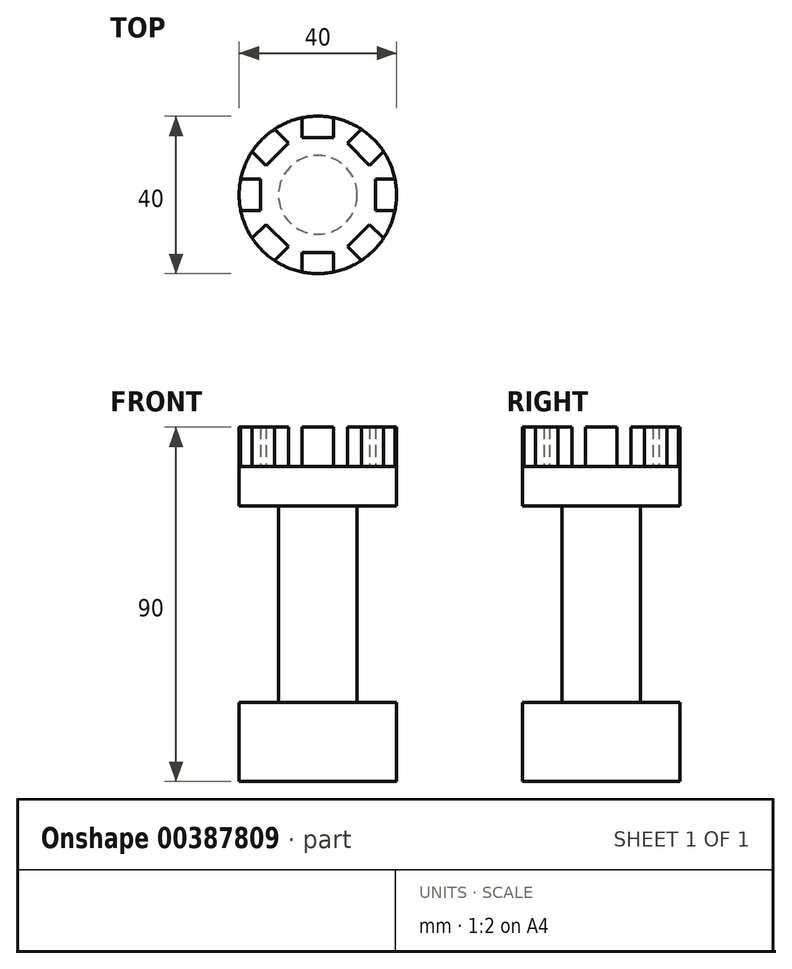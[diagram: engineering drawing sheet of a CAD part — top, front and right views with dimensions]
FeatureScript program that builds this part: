
annotation { "Feature Type Name" : "Feature", "Feature Type Description" : "" }
export const myFeature = defineFeature(function(context is Context, id is Id, definition is map)
    precondition{}
    {
        {
            var Q0;
            Q0=qCreatedBy(makeId("Front.planeOp"),FACE);
            var sketch = newSketch(context, id + "F0", { "sketchPlane" : qUnion([Q0])});
            skLineSegment(sketch, "E0", {"start": v(0, 64.98) * mm, "end": v(0, -64.38) * mm, "construction": true});
            skLineSegment(sketch, "E1", {"start": v(0, 40) * mm, "end": v(20, 40) * mm});
            skLineSegment(sketch, "E2", {"start": v(20, 30) * mm, "end": v(10, 30) * mm});
            skLineSegment(sketch, "E3", {"start": v(10, 30) * mm, "end": v(10, -20) * mm});
            skLineSegment(sketch, "E4", {"start": v(10, -20) * mm, "end": v(20, -20) * mm});
            skLineSegment(sketch, "E5", {"start": v(20, -20) * mm, "end": v(20, -40) * mm});
            skLineSegment(sketch, "E6", {"start": v(20, -40) * mm, "end": v(0, -40) * mm});
            skLineSegment(sketch, "E7", {"start": v(0, -40) * mm, "end": v(0, 40) * mm});
            skLineSegment(sketch, "E8", {"start": v(0, 40) * mm, "end": v(0, 40) * mm});
            skLineSegment(sketch, "E9", {"start": v(20, 40) * mm, "end": v(20, 30) * mm});
            skSolve(sketch);
        }
        {
            var Q0;
            Q0 = qSketchRegion(id + "F0", true);
            var Q1;
            Q1=sQuery(id+"F0.wireOp",EDGE,"E0");
            revolve(context, id + "F1", {"entities" : qUnion([Q0]), "axis" : qUnion([Q1]), "revolveType" : RevolveType.FULL});
        }
        {
            var Q0;
            Q0=makeQuery(id+"F1.opRevolve","SWEPT_FACE",FACE,{"disambiguationData":[OSD([sQuery(id+"F0.wireOp",EDGE,"E1")])]});
            var sketch = newSketch(context, id + "F2", { "sketchPlane" : qUnion([Q0])});
            skLineSegment(sketch, "E10", {"start": v(-4, 19.6) * mm, "end": v(-4, 14.6) * mm});
            skLineSegment(sketch, "E11", {"start": v(-4, 14.6) * mm, "end": v(4, 14.6) * mm});
            skLineSegment(sketch, "E12", {"start": v(4, 14.6) * mm, "end": v(4, 19.6) * mm});
            skArc(sketch, "E13", {"start": v(4, 19.6) * mm, "mid": v(0, 20) * mm, "end": v(-4, 19.6) * mm});
            skSolve(sketch);
        }
        {
            var Q0;
            Q0 = qSketchRegion(id + "F2", true);
            extrude(context, id + "F3", {"entities" : qUnion([Q0]), "operationType" : NewBodyOperationType.ADD, "depth" : 10 * mm});
        }
        {
            var Q0;
            Q0=makeQuery(id+"F1.opRevolve","SWEPT_BODY",BODY,{"disambiguationData":[OSD([sQuery(id+"F0.wireOp",EDGE,"E1"),sQuery(id+"F0.wireOp",EDGE,"E2"),sQuery(id+"F0.wireOp",EDGE,"E3"),sQuery(id+"F0.wireOp",EDGE,"E4"),sQuery(id+"F0.wireOp",EDGE,"E5"),sQuery(id+"F0.wireOp",EDGE,"E6"),sQuery(id+"F0.wireOp",EDGE,"E7"),sQuery(id+"F0.wireOp",EDGE,"E9")])]});
            var Q1;
            Q1=makeQuery(id+"F3.boolean.opBoolean","MERGE",FACE,{"derivedFrom":[makeQuery(id+"F1.opRevolve","SWEPT_FACE",FACE,{"disambiguationData":[OSD([sQuery(id+"F0.wireOp",EDGE,"E9")])]}),makeQuery(id+"F3.opExtrude","SWEPT_FACE",FACE,{"disambiguationData":[OSD([sQuery(id+"F2.wireOp",EDGE,"E13")])]})]});
            circularPattern(context, id + "F4", {"entities" : qUnion([Q0]), "axis" : qUnion([Q1]), "angle" : 360 * degree, "instanceCount" : 8, "equalSpace" : true});
        }
    });
